# Revit family: Park Sofa Ekeby CC
name_source: partatom
category: Furniture
units: mm (PartAtom-declared; Revit-internal decimal feet)

## family parameters
Always vertical = Yes
Cut with Voids When Loaded = No
OmniClass Number = 23.21.23.13.15
Room Calculation Point = No
Shared = No
Work Plane-Based = No

## types (7) — shared parameters
BIMobject category = Bench & Park Bench
Description = Park Sofa Ekeby
Edition number = 1
IFC Classification = Furniture
Manufacturer = Hags
Manufacturer name = HAGS
OmniClass Code = 23-21 23 13 15
OmniClass Description = Residential Sofas
Product Guid = 90e49432-c870-4a59-897e-b15016e8f9bd
Product SKU = Bench_Ekeby_Detached
QR code = https://www.hags.com
URL = https://www.hags.com
Uniclass 1.4 Code = L8211
Uniclass 1.4 Description = Furniture
zero-valued in all types: Default Elevation

## per-type parameters (varying)
| type | Body material | Body material_90 | Construction material | Model | Product data url | Product name | Product url |
| 8037002 Bark Brown / Black | Hags - Wood - Bark brown | Hags - Wood - Bark brown 90 | Hags - Steel - Powder coated - Black |  |  | Ekeby Park Bench |  |
| 8037013 Bark Brown/ Galvanized | Hags - Wood - Bark brown | Hags - Wood - Bark brown 90 | Hags - Steel - Galvanized |  | https://bimobject.com | Ekeby Bench | https://hags.se |
| 8037018 Green / Black | Hags - Steel - Powder coated - Green | Hags - Steel - Powder coated - Green | Hags - Steel - Powder coated - Black |  | https://bimobject.com | Park Bench Ekeby | https://hags.se |
| 8058441 Hardwood / Galvanised | Hags - Hard Wood | Hags - Bilinga | Hags - Steel - Galvanized | 8058441 |  | Ekeby Park Bench | https://www.hags.com |
| 8064354 Recycled Plastic / Galvanised | Hags - Recycled Plastic | Hags - Recycled Plastic | Hags - Steel - Galvanized | 8037012 | https://bimobject.com | Ekeby Park Bench | https://hags.se |
| 8064352 Recycled Plastic / Black | Hags - Recycled Plastic | Hags - Recycled Plastic | Hags - Steel - Powder coated - Black |  |  | Ekeby Park Bench |  |
| 8058458 Hardwood / Black | Hags - Hard Wood | Hags - Hard Wood | Hags - Steel - Powder coated - Black | 8058458 |  | Ekeby Park Bench | https://www.hags.com |

## geometry (parser evidence)
native form markers: Sweep x3
no freeform markers — native parametric forms only
